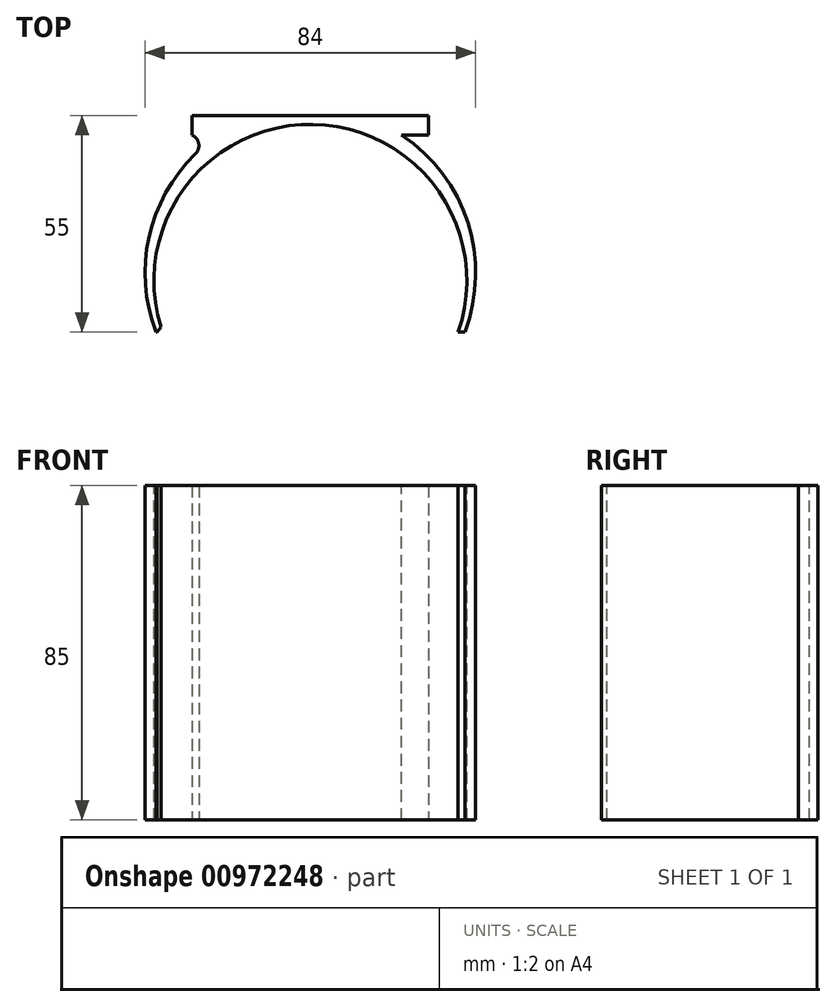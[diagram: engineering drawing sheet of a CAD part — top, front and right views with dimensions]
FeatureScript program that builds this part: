
annotation { "Feature Type Name" : "Feature", "Feature Type Description" : "" }
export const myFeature = defineFeature(function(context is Context, id is Id, definition is map)
    precondition{}
    {
        {
            var Q0;
            Q0=qCreatedBy(makeId("Front.planeOp"),FACE);
            var sketch = newSketch(context, id + "F0", { "sketchPlane" : qUnion([Q0])});
            skLineSegment(sketch, "E0.bottom", {"start": v(30, 42.5) * mm, "end": v(-30, 42.5) * mm});
            skLineSegment(sketch, "E0.top", {"start": v(30, -42.5) * mm, "end": v(-30, -42.5) * mm});
            skLineSegment(sketch, "E0.left", {"start": v(30, 42.5) * mm, "end": v(30, -42.5) * mm});
            skLineSegment(sketch, "E0.right", {"start": v(-30, 42.5) * mm, "end": v(-30, -42.5) * mm});
            skPoint(sketch, "E0.middle", {"position": v(0, 0) * mm});
            skSolve(sketch);
        }
        {
            var Q0;
            Q0 = qSketchRegion(id + "F0", true);
            extrude(context, id + "F1", {"entities" : qUnion([Q0]), "depth" : 5 * mm, "offsetDistance" : 25 * mm});
        }
        {
            var Q0;
            Q0=makeQuery(id+"F1.opExtrude","SWEPT_FACE",FACE,{"disambiguationData":[OSD([sQuery(id+"F0.wireOp",EDGE,"E0.bottom")])]});
            var sketch = newSketch(context, id + "F2", { "sketchPlane" : qUnion([Q0])});
            skArc(sketch, "E1", {"start": v(-23.22, -5) * mm, "mid": v(-40, -27.19) * mm, "end": v(-39.23, -55) * mm});
            skLineSegment(sketch, "E2.0", {"start": v(30, -5) * mm, "end": v(-30, -5) * mm});
            skPoint(sketch, "E3.0", {"position": v(0, 0) * mm});
            skLineSegment(sketch, "E4", {"start": v(-23.22, -5) * mm, "end": v(-30, -5) * mm});
            skLineSegment(sketch, "E5", {"start": v(-30, -5) * mm, "end": v(23.22, -5) * mm});
            skArc(sketch, "E6", {"start": v(37.56, -55) * mm, "mid": v(0, -2.25) * mm, "end": v(-37.56, -55) * mm});
            skLineSegment(sketch, "E7", {"start": v(39.23, -55) * mm, "end": v(-39.23, -55) * mm});
            skArc(sketch, "E8.trimOffspring", {"start": v(39.23, -55) * mm, "mid": v(40, -27.19) * mm, "end": v(23.22, -5) * mm});
            skSolve(sketch);
        }
        {
            var Q0;
            {var subQ0=sQuery(id+"F2.wireOp",EDGE,"E6");var subQ1=sQuery(id+"F2.wireOp",EDGE,"E2.0");var subQ2=makeQuery(id+"F2.imprint","INTERSECT",VERTEX,{"disambiguationData":[OD(0.0)],"derivedFrom":[subQ1,subQ0]});var subQ4=makeQuery(id+"F2.imprint","IMPRINT",EDGE,{"disambiguationData":[TD([[subQ2,-1.0]])],"derivedFrom":subQ1});var subQ10=sQuery(id+"F2.wireOp",EDGE,"E8.trimOffspring");var subQ11=sQuery(id+"F2.wireOp",EDGE,"E1");Q0=qUnion([makeQuery(id+"F2.imprint","IMPRINT",FACE,{"disambiguationData":[TD([[makeQuery(id+"F2.imprint","IMPRINT",EDGE,{"derivedFrom":subQ11}),1.0]])]}),makeQuery(id+"F2.imprint","IMPRINT",FACE,{"disambiguationData":[TD([[makeQuery(id+"F2.imprint","IMPRINT",EDGE,{"derivedFrom":subQ10}),1.0]])]}),makeQuery(id+"F2.imprint","IMPRINT",FACE,{"disambiguationData":[TD([[subQ4,-1.0]])]}),makeQuery(id+"F2.imprint","IMPRINT",FACE,{"disambiguationData":[TD([[subQ4,1.0]])]})]);}
            var Q1;
            Q1=makeQuery(id+"F1.opExtrude","SWEPT_FACE",FACE,{"disambiguationData":[OSD([sQuery(id+"F0.wireOp",EDGE,"E0.top")])]});
            extrude(context, id + "F3", {"entities" : qUnion([Q0]), "operationType" : NewBodyOperationType.ADD, "endBound" : BoundingType.UP_TO_SURFACE, "oppositeDirection" : true, "depth" : 25 * mm, "endBoundEntityFace" : qUnion([Q1]), "offsetDistance" : 25 * mm});
        }
        {
            var Q0;
            {var subQ0=sQuery(id+"F2.wireOp",EDGE,"E6");var subQ1=sQuery(id+"F2.wireOp",EDGE,"E2.0");var subQ2=makeQuery(id+"F2.imprint","INTERSECT",VERTEX,{"disambiguationData":[OD(0.0)],"derivedFrom":[subQ1,subQ0]});Q0=makeQuery(id+"F2.imprint","IMPRINT",FACE,{"disambiguationData":[TD([[makeQuery(id+"F2.imprint","IMPRINT",EDGE,{"disambiguationData":[TD([[subQ2,-1.0]])],"derivedFrom":subQ1}),1.0]])]});}
            var Q1;
            {var subQ0=sQuery(id+"F2.wireOp",EDGE,"E6");var subQ1=sQuery(id+"F2.wireOp",EDGE,"E2.0");var subQ2=makeQuery(id+"F2.imprint","INTERSECT",VERTEX,{"disambiguationData":[OD(0.0)],"derivedFrom":[subQ1,subQ0]});Q1=makeQuery(id+"F2.imprint","IMPRINT",FACE,{"disambiguationData":[TD([[makeQuery(id+"F2.imprint","IMPRINT",EDGE,{"disambiguationData":[TD([[subQ2,-1.0]])],"derivedFrom":subQ1}),-1.0]])]});}
            extrude(context, id + "F4", {"entities" : qUnion([Q0, Q1]), "operationType" : NewBodyOperationType.REMOVE, "endBound" : BoundingType.UP_TO_NEXT, "oppositeDirection" : true, "depth" : 25 * mm, "offsetDistance" : 25 * mm});
        }
        {
            var Q0;
            Q0=makeQuery(id+"F3.opExtrude","SWEPT_EDGE",EDGE,{"disambiguationData":[OSD([sQuery(id+"F2.wireOp",EDGE,"E2.0"),sQuery(id+"F2.wireOp",EDGE,"E8.trimOffspring")])]});
            var Q1;
            Q1=makeQuery(id+"F3.opExtrude","SWEPT_EDGE",EDGE,{"disambiguationData":[OSD([sQuery(id+"F2.wireOp",EDGE,"E1"),sQuery(id+"F2.wireOp",EDGE,"E2.0")])]});
            fillet(context, id + "F5", {"entities" : qUnion([Q0, Q1]), "radius" : 3 * mm, "tangentPropagation" : true, "allowEdgeOverflow" : false});
        }
        {
            var Q0;
            {var subQ0=sQuery(id+"F2.wireOp",EDGE,"E7");var subQ1=sQuery(id+"F2.wireOp",EDGE,"E6");Q0=makeQuery(id+"F4.boolean.opBoolean","COPY",EDGE,{"derivedFrom":makeQuery(id+"F4.opExtrude","SWEPT_EDGE",EDGE,{"disambiguationData":[OSD([subQ1,subQ0]),TDD([makeQuery(id+"F2.imprint","INTERSECT",VERTEX,{"disambiguationData":[OD(1.0)],"derivedFrom":[subQ1,subQ0]})])]})});}
            var Q1;
            {var subQ0=sQuery(id+"F2.wireOp",EDGE,"E7");var subQ1=sQuery(id+"F2.wireOp",EDGE,"E6");Q1=makeQuery(id+"F4.boolean.opBoolean","COPY",EDGE,{"derivedFrom":makeQuery(id+"F4.opExtrude","SWEPT_EDGE",EDGE,{"disambiguationData":[OSD([subQ1,subQ0]),TDD([makeQuery(id+"F2.imprint","INTERSECT",VERTEX,{"disambiguationData":[OD(0.0)],"derivedFrom":[subQ1,subQ0]})])]})});}
            chamfer(context, id + "F6", {"entities" : qUnion([Q0, Q1]), "width" : 1 * mm, "tangentPropagation" : true});
        }
    });
